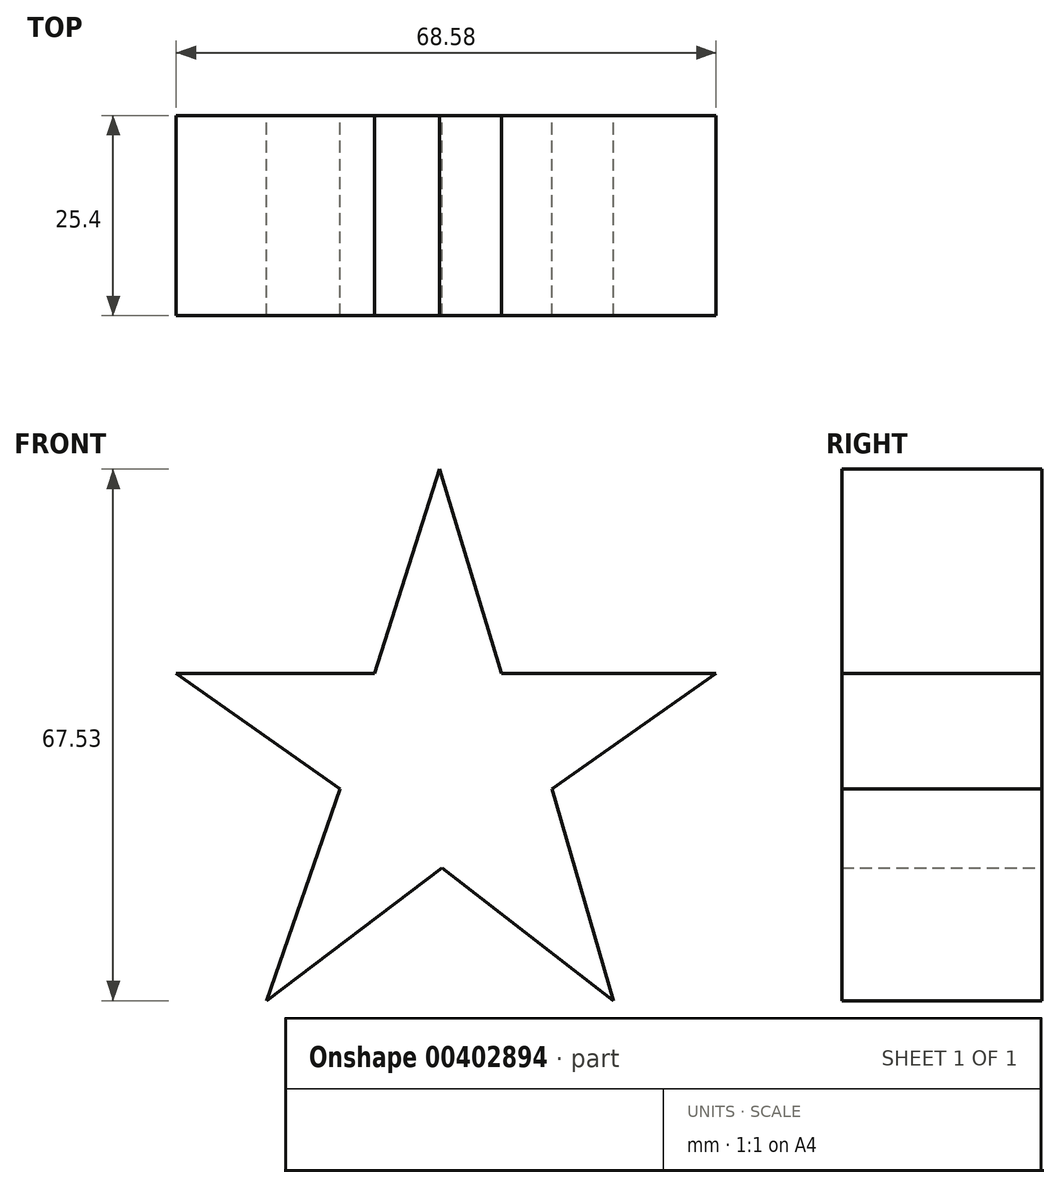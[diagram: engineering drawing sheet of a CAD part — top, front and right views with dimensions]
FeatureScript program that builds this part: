
annotation { "Feature Type Name" : "Feature", "Feature Type Description" : "" }
export const myFeature = defineFeature(function(context is Context, id is Id, definition is map)
    precondition{}
    {
        {
            var Q0;
            Q0=qCreatedBy(makeId("Front.planeOp"),FACE);
            var sketch = newSketch(context, id + "F0", { "sketchPlane" : qUnion([Q0])});
            skLineSegment(sketch, "E0", {"start": v(-27.65, 9.05) * mm, "end": v(-2.45, 9.05) * mm});
            skLineSegment(sketch, "E1", {"start": v(-2.45, 9.05) * mm, "end": v(5.79, 34.99) * mm});
            skLineSegment(sketch, "E2", {"start": v(5.79, 34.99) * mm, "end": v(13.7, 9.05) * mm});
            skLineSegment(sketch, "E3", {"start": v(13.7, 9.05) * mm, "end": v(40.93, 9.05) * mm});
            skLineSegment(sketch, "E4", {"start": v(40.93, 9.05) * mm, "end": v(20.06, -5.63) * mm});
            skLineSegment(sketch, "E5", {"start": v(20.06, -5.63) * mm, "end": v(27.9, -32.54) * mm});
            skLineSegment(sketch, "E6", {"start": v(27.9, -32.54) * mm, "end": v(6.12, -15.66) * mm});
            skLineSegment(sketch, "E7", {"start": v(6.12, -15.66) * mm, "end": v(-16.15, -32.54) * mm});
            skLineSegment(sketch, "E8", {"start": v(-16.15, -32.54) * mm, "end": v(-6.85, -5.63) * mm});
            skLineSegment(sketch, "E9", {"start": v(-6.85, -5.63) * mm, "end": v(-27.65, 9.05) * mm});
            skSolve(sketch);
        }
        {
            var Q0;
            Q0=makeQuery(id+"F0.imprint","IMPRINT",FACE,{"disambiguationData":[TD([[makeQuery(id+"F0.imprint","IMPRINT",EDGE,{"derivedFrom":sQuery(id+"F0.wireOp",EDGE,"E0")}),-1.0]])]});
            extrude(context, id + "F1", {"entities" : qUnion([Q0]), "depth" : 25.4 * mm});
        }
    });
